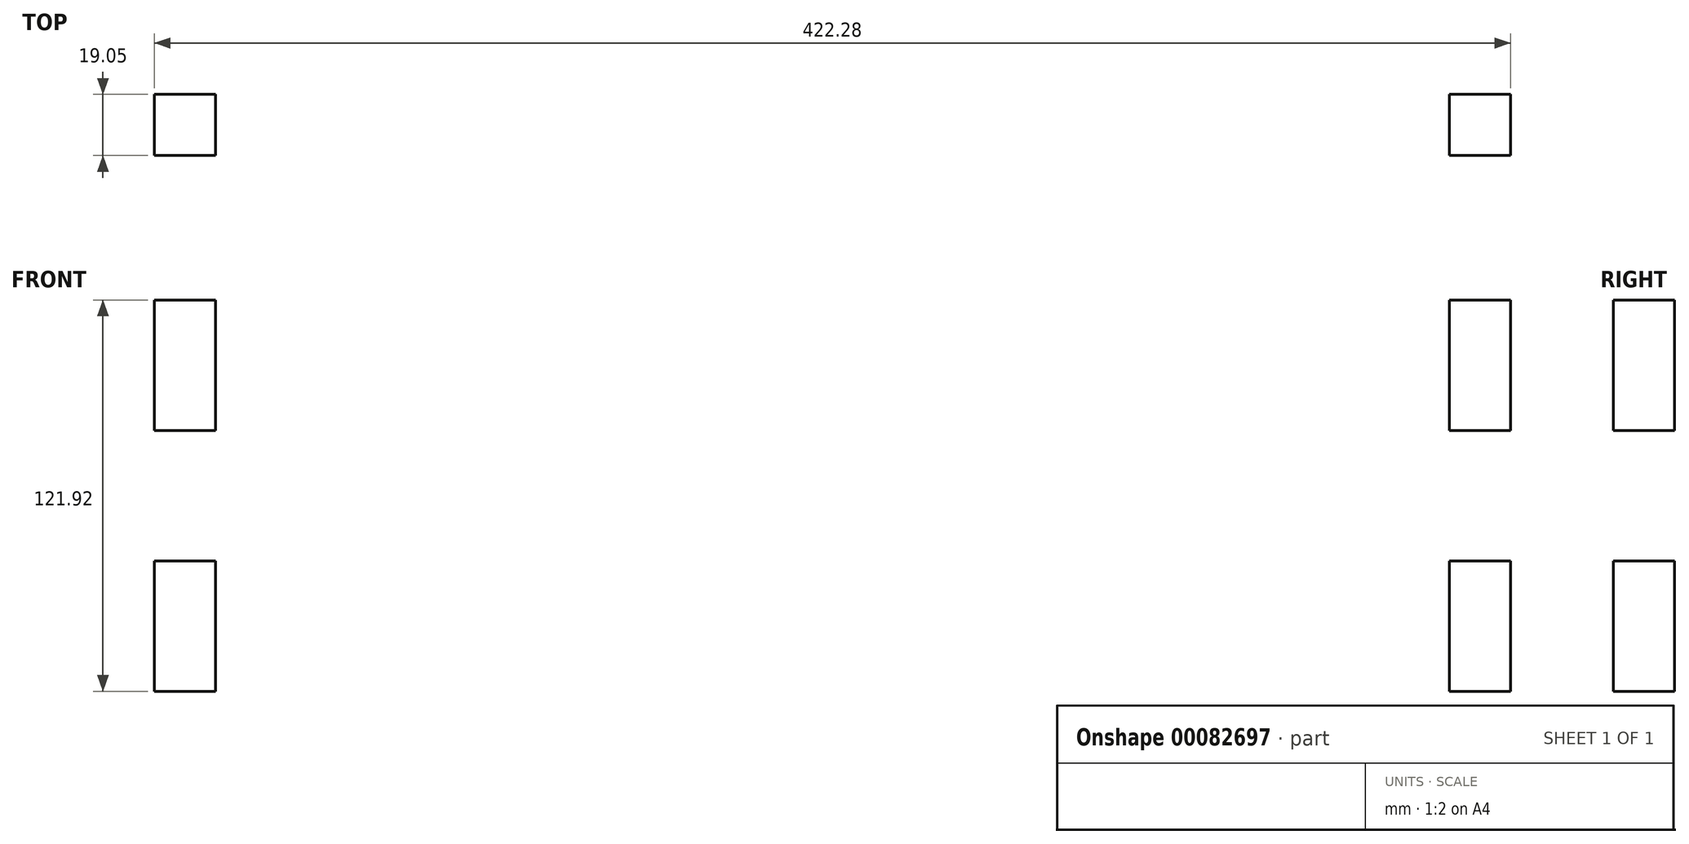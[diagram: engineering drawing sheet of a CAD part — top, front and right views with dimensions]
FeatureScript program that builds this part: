
annotation { "Feature Type Name" : "Feature", "Feature Type Description" : "" }
export const myFeature = defineFeature(function(context is Context, id is Id, definition is map)
    precondition{}
    {
        {
            var Q0;
            Q0=qCreatedBy(makeId("Front.planeOp"),FACE);
            var sketch = newSketch(context, id + "F0", { "sketchPlane" : qUnion([Q0])});
            skLineSegment(sketch, "E0", {"start": v(-128.3, 67.17) * mm, "end": v(293.98, 67.17) * mm});
            skLineSegment(sketch, "E1", {"start": v(-128.3, 67.17) * mm, "end": v(-128.3, -101.1) * mm});
            skLineSegment(sketch, "E2", {"start": v(-128.3, -101.1) * mm, "end": v(293.98, -101.1) * mm});
            skLineSegment(sketch, "E3", {"start": v(293.98, 67.17) * mm, "end": v(293.98, -101.1) * mm});
            skLineSegment(sketch, "E4.bottom", {"start": v(-128.3, 67.17) * mm, "end": v(-109.25, 67.17) * mm});
            skLineSegment(sketch, "E4.top", {"start": v(-128.3, 26.53) * mm, "end": v(-109.25, 26.53) * mm});
            skLineSegment(sketch, "E4.left", {"start": v(-128.3, 67.17) * mm, "end": v(-128.3, 26.53) * mm});
            skLineSegment(sketch, "E4.right", {"start": v(-109.25, 67.17) * mm, "end": v(-109.25, 26.53) * mm});
            skLineSegment(sketch, "E5", {"start": v(82.84, 67.17) * mm, "end": v(82.84, -101.1) * mm, "construction": true});
            skLineSegment(sketch, "E6.top", {"start": v(-128.3, -14.1) * mm, "end": v(-109.25, -14.1) * mm});
            skLineSegment(sketch, "E6.left", {"start": v(-128.3, 26.53) * mm, "end": v(-128.3, -14.1) * mm});
            skLineSegment(sketch, "E6.right", {"start": v(-109.25, 26.53) * mm, "end": v(-109.25, -14.1) * mm});
            skLineSegment(sketch, "E7.top", {"start": v(-128.3, -54.75) * mm, "end": v(-109.25, -54.75) * mm});
            skLineSegment(sketch, "E7.left", {"start": v(-128.3, -14.1) * mm, "end": v(-128.3, -54.75) * mm});
            skLineSegment(sketch, "E7.right", {"start": v(-109.25, -14.1) * mm, "end": v(-109.25, -54.75) * mm});
            skLineSegment(sketch, "E8", {"start": v(-109.25, -101.1) * mm, "end": v(-109.25, -54.75) * mm});
            skLineSegment(sketch, "E9", {"start": v(-128.3, -101.1) * mm, "end": v(-109.25, -101.1) * mm});
            skLineSegment(sketch, "E10.MirrorCS", {"start": v(293.98, -14.1) * mm, "end": v(274.93, -14.1) * mm});
            skLineSegment(sketch, "E11.MirrorCS", {"start": v(293.98, 26.53) * mm, "end": v(274.93, 26.53) * mm});
            skLineSegment(sketch, "E12.MirrorCS", {"start": v(293.98, 67.17) * mm, "end": v(274.93, 67.17) * mm});
            skLineSegment(sketch, "E13.MirrorCS", {"start": v(293.98, -101.1) * mm, "end": v(274.93, -101.1) * mm});
            skLineSegment(sketch, "E14.MirrorCS", {"start": v(293.98, -54.75) * mm, "end": v(274.93, -54.75) * mm});
            skLineSegment(sketch, "E15.MirrorCS", {"start": v(293.98, -14.1) * mm, "end": v(293.98, -54.75) * mm});
            skLineSegment(sketch, "E16.MirrorCS", {"start": v(274.93, -14.1) * mm, "end": v(274.93, -54.75) * mm});
            skLineSegment(sketch, "E17.MirrorCS", {"start": v(274.93, -101.1) * mm, "end": v(274.93, -54.75) * mm});
            skLineSegment(sketch, "E18.MirrorCS", {"start": v(274.93, 26.53) * mm, "end": v(274.93, -14.1) * mm});
            skLineSegment(sketch, "E19.MirrorCS", {"start": v(293.98, 67.17) * mm, "end": v(293.98, 26.53) * mm});
            skLineSegment(sketch, "E20.MirrorCS", {"start": v(274.93, 67.17) * mm, "end": v(274.93, 26.53) * mm});
            skLineSegment(sketch, "E21.MirrorCS", {"start": v(293.98, 26.53) * mm, "end": v(293.98, -14.1) * mm});
            skSolve(sketch);
        }
        {
            var Q0;
            Q0=makeQuery(id+"F0.imprint","IMPRINT",FACE,{"disambiguationData":[TD([[makeQuery(id+"F0.imprint","IMPRINT",EDGE,{"derivedFrom":sQuery(id+"F0.wireOp",EDGE,"E4.bottom")}),-1.0]])]});
            var Q1;
            Q1=makeQuery(id+"F0.imprint","IMPRINT",FACE,{"disambiguationData":[TD([[makeQuery(id+"F0.imprint","IMPRINT",EDGE,{"derivedFrom":sQuery(id+"F0.wireOp",EDGE,"E11.MirrorCS")}),-1.0]])]});
            var Q2;
            Q2=makeQuery(id+"F0.imprint","IMPRINT",FACE,{"disambiguationData":[TD([[makeQuery(id+"F0.imprint","IMPRINT",EDGE,{"derivedFrom":sQuery(id+"F0.wireOp",EDGE,"E6.top")}),-1.0]])]});
            var Q3;
            {var subQ0=sQuery(id+"F0.wireOp",EDGE,"E10.MirrorCS");Q3=makeQuery(id+"F0.imprint","IMPRINT",FACE,{"disambiguationData":[TD([[makeQuery(id+"F0.imprint","IMPRINT",EDGE,{"derivedFrom":subQ0}),1.0]])]});}
            var Q4;
            Q4=makeQuery(id+"F0.imprint","IMPRINT",FACE,{"disambiguationData":[TD([[makeQuery(id+"F0.imprint","IMPRINT",EDGE,{"derivedFrom":sQuery(id+"F0.wireOp",EDGE,"E0")}),-1.0]])]});
            extrude(context, id + "F1", {"entities" : qUnion([Q0, Q1, Q2, Q3, Q4]), "depth" : 19.05 * mm});
        }
    });
